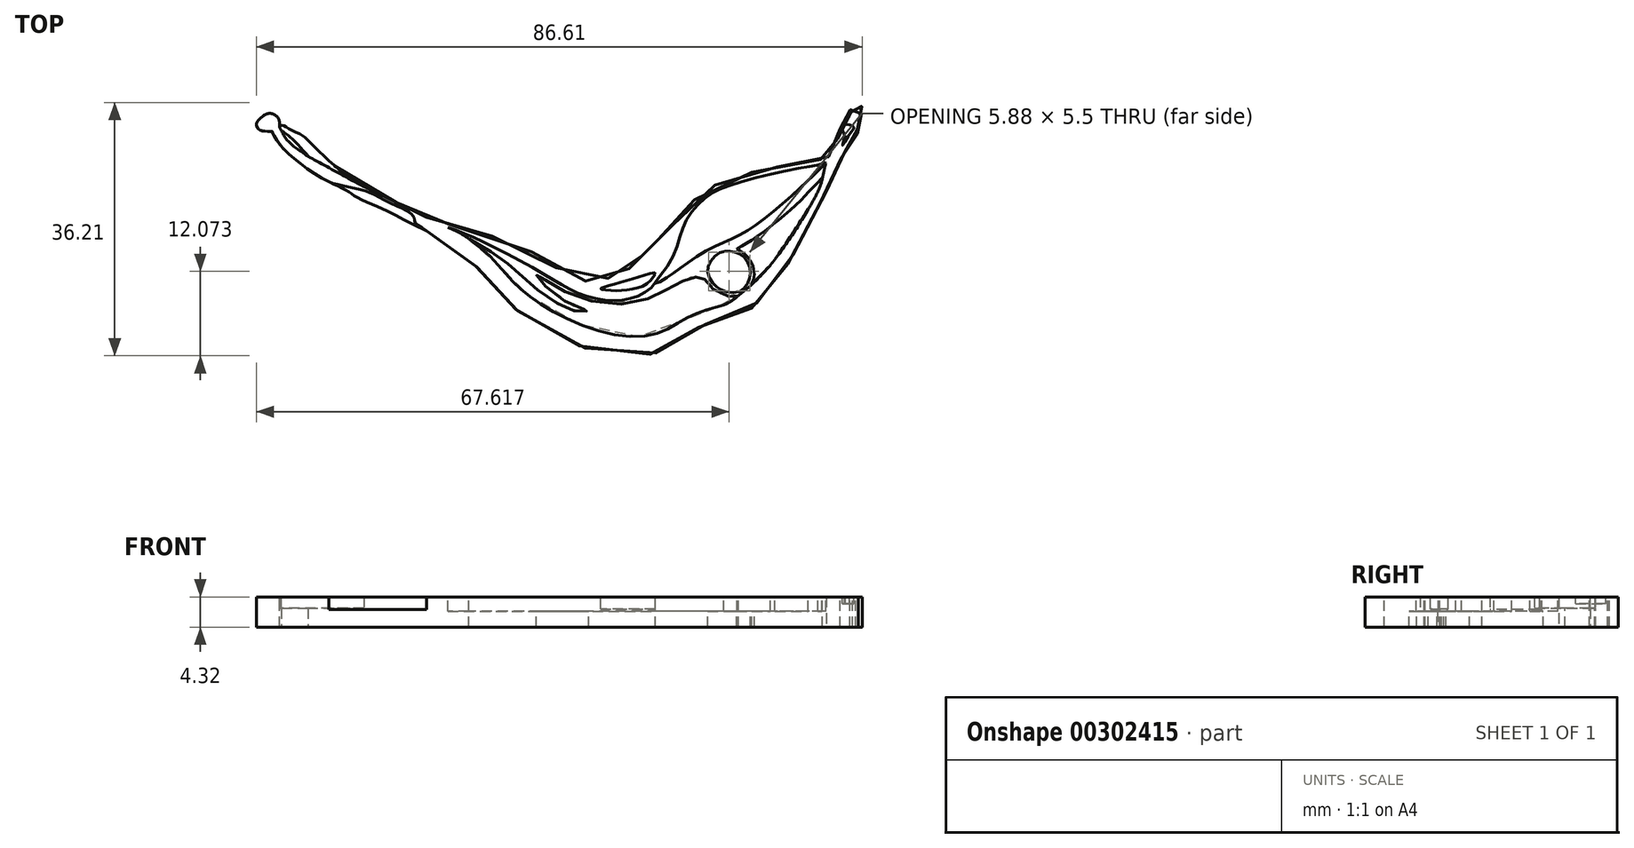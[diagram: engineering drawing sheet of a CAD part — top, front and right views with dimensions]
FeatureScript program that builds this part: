
annotation { "Feature Type Name" : "Feature", "Feature Type Description" : "" }
export const myFeature = defineFeature(function(context is Context, id is Id, definition is map)
    precondition{}
    {
        {
            var Q0;
            Q0=qCreatedBy(makeId("Top.planeOp"),FACE);
            var sketch = newSketch(context, id + "F0", { "sketchPlane" : qUnion([Q0])});
            skFitSpline(sketch, "E0", {"points": [v(-43.46, 14.38) * mm, v(-44.23, 13.82) * mm, v(-44.8, 13.18) * mm, v(-44.82, 12.68) * mm, v(-44.36, 12.07) * mm, v(-43.25, 11.92) * mm, v(-42.68, 11.9) * mm, v(-42.57, 11.9) * mm, v(-42.53, 11.75) * mm, v(-41.7, 10.3) * mm, v(-39.3, 7.87) * mm, v(-34.59, 4.74) * mm, v(-31.85, 3.4) * mm, v(-30.37, 2.4) * mm, v(-26.53, 0.67) * mm, v(-23.64, -0.81) * mm, v(-20.37, -2.4) * mm, v(-17.35, -4.13) * mm, v(-13.45, -7.38) * mm, v(-9.8, -11.5) * mm, v(-7.92, -13.38) * mm, v(-5.1, -15.68) * mm, v(2.66, -19.24) * mm, v(8.89, -20.2) * mm, v(13.19, -19.5) * mm, v(16.5, -17.42) * mm, v(19.24, -15.76) * mm, v(23.96, -14.69) * mm, v(26.11, -13.28) * mm, v(28.6, -10.38) * mm, v(30.9, -7.42) * mm, v(33.51, -2.7) * mm, v(36.14, 2.38) * mm, v(38, 6.37) * mm, v(38.5, 7.84) * mm, v(39, 8.38) * mm, v(39.55, 9.56) * mm, v(40.04, 10.09) * mm, v(40.35, 11.03) * mm, v(41.15, 11.69) * mm, v(41.15, 11.97) * mm, v(40.9, 12.98) * mm, v(40.84, 13.54) * mm, v(40.94, 13.74) * mm, v(41.47, 14.13) * mm, v(41.74, 14.96) * mm, v(41.54, 15.76) * mm, v(40.73, 16) * mm, v(40.18, 15.73) * mm, v(40, 15.17) * mm, v(40.25, 14.82) * mm, v(40.39, 14.68) * mm, v(39.83, 14.68) * mm, v(39.2, 13.81) * mm, v(38.64, 12.7) * mm, v(38.57, 11.58) * mm, v(37.8, 10.12) * mm, v(37.42, 9.29) * mm, v(37.15, 8.48) * mm, v(36.8, 8.2) * mm, v(36.24, 8) * mm, v(32.93, 7.44) * mm, v(26.45, 6.18) * mm, v(22.34, 5) * mm, v(18.2, 2.44) * mm, v(15.35, -0.53) * mm, v(13.74, -2.57) * mm, v(11.52, -4.5) * mm, v(10.67, -5.35) * mm, v(9.53, -6.82) * mm, v(7.86, -8.1) * mm, v(6.39, -8.84) * mm, v(3.57, -9.5) * mm, v(0.75, -9.15) * mm, v(-3.47, -6.61) * mm, v(-7.61, -4.31) * mm, v(-16.63, -1.54) * mm, v(-19.79, -0.7) * mm, v(-23.14, 0.88) * mm, v(-29.1, 3.83) * mm, v(-33.31, 6.66) * mm, v(-37.33, 10.5) * mm, v(-38.62, 11.54) * mm, v(-40.4, 12.37) * mm, v(-41.2, 12.78) * mm, v(-41.53, 12.66) * mm, v(-41.53, 12.96) * mm, v(-41.76, 13.84) * mm, v(-42.64, 14.43) * mm, v(-43.46, 14.38) * mm]});
            skFitSpline(sketch, "E1", {"points": [v(-14.45, -3.47) * mm, v(-11.98, -5.47) * mm, v(-8.6, -9.16) * mm, v(-4.78, -12.4) * mm, v(3.52, -16.48) * mm, v(11.92, -17.15) * mm, v(16.23, -15.05) * mm, v(20, -13.5) * mm, v(22.54, -12.67) * mm, v(23.7, -11.87) * mm, v(24.06, -11.6) * mm, v(23.7, -11.71) * mm, v(23.36, -11.76) * mm, v(22.28, -11.66) * mm, v(20.73, -10.86) * mm, v(19.84, -10.07) * mm, v(19.35, -9.27) * mm, v(19.1, -9.24) * mm, v(18.81, -9.13) * mm, v(18.34, -8.96) * mm, v(17.72, -8.93) * mm, v(16.78, -9.06) * mm, v(15.52, -9.94) * mm, v(13.74, -10.75) * mm, v(12.14, -11.6) * mm, v(9.16, -12.63) * mm, v(4.7, -12.7) * mm, v(0.45, -11.54) * mm, v(-2.41, -10.03) * mm, v(-4.02, -9.05) * mm, v(-4.68, -8.62) * mm, v(-4.8, -8.64) * mm, v(-4.78, -8.75) * mm, v(-4.2, -9.48) * mm, v(-3.27, -10.53) * mm, v(-0.57, -12.48) * mm, v(1.68, -13.47) * mm, v(2.44, -13.62) * mm, v(2.56, -13.66) * mm, v(2.63, -13.74) * mm, v(2.54, -13.8) * mm, v(2.23, -13.85) * mm, v(1.72, -13.87) * mm, v(0.62, -13.77) * mm, v(-0.47, -13.35) * mm, v(-2.89, -12.12) * mm, v(-5.08, -10.42) * mm, v(-6.62, -9.1) * mm, v(-7.7, -7.93) * mm, v(-9.64, -6.52) * mm, v(-11.55, -5.11) * mm, v(-14.45, -3.47) * mm]});
            skFitSpline(sketch, "E2", {"points": [v(12.2, -9.81) * mm, v(14.18, -7) * mm, v(15.74, -3.08) * mm, v(17.1, 0) * mm, v(19.55, 2.56) * mm, v(22.34, 4.02) * mm, v(30.1, 6.1) * mm, v(35.1, 7.05) * mm, v(36.11, 7.31) * mm, v(36.51, 7.45) * mm, v(36.62, 7.48) * mm, v(36.54, 7.38) * mm, v(35.62, 6.44) * mm, v(34.13, 5) * mm, v(30.47, 1.6) * mm, v(26.26, -1.68) * mm, v(23.17, -3.45) * mm, v(19.85, -4.99) * mm, v(15.96, -7.51) * mm, v(13.72, -9.06) * mm, v(12.2, -9.81) * mm]});
            skFitSpline(sketch, "E3", {"points": [v(23.8, -4.96) * mm, v(24.13, -5.1) * mm, v(25.71, -6.5) * mm, v(26.28, -8.03) * mm, v(26.22, -9.26) * mm, v(25.98, -9.9) * mm, v(26.37, -9.55) * mm, v(28.15, -7.77) * mm, v(29.91, -5.54) * mm, v(32.05, -2.29) * mm, v(34.42, 1.4) * mm, v(35.71, 3.98) * mm, v(36.04, 5.01) * mm, v(36.07, 5.2) * mm, v(36.07, 5.3) * mm, v(35.97, 5.22) * mm, v(35.8, 5.01) * mm, v(34.73, 3.9) * mm, v(32.75, 1.82) * mm, v(28.99, -1.45) * mm, v(27.07, -2.89) * mm, v(24.53, -4.52) * mm, v(23.8, -4.96) * mm]});
            skFitSpline(sketch, "E4", {"points": [v(23.56, -5.38) * mm, v(24.75, -5.97) * mm, v(25.7, -7.5) * mm, v(25.71, -8.83) * mm, v(25.2, -10.15) * mm, v(23.8, -11.15) * mm, v(21.76, -10.81) * mm, v(20.69, -10.11) * mm, v(19.78, -8.74) * mm, v(19.86, -7.13) * mm, v(21.02, -5.68) * mm, v(22.4, -5.25) * mm, v(23.56, -5.38) * mm]});
            skFitSpline(sketch, "E5", {"points": [v(-37.48, 8.36) * mm, v(-38.4, 9) * mm, v(-39.47, 9.7) * mm, v(-40.17, 10.38) * mm, v(-40.78, 11.08) * mm, v(-41.2, 11.88) * mm, v(-41.26, 11.99) * mm, v(-41.14, 11.94) * mm, v(-40.59, 11.5) * mm, v(-39.83, 10.94) * mm, v(-38.98, 10.06) * mm, v(-37.87, 8.86) * mm, v(-37.48, 8.36) * mm]});
            skSolve(sketch);
        }
        {
            var Q0;
            Q0=qSketchRegion(id+"F0",true);
            extrude(context, id + "F1", {"entities" : qUnion([Q0]), "depth" : 4.32 * mm});
        }
        {
            var Q0;
            Q0=makeQuery(id+"F1.opExtrude","CAP_FACE",FACE,{"disambiguationData":[OSD([sQuery(id+"F0.wireOp",EDGE,"E0"),sQuery(id+"F0.wireOp",EDGE,"E1"),sQuery(id+"F0.wireOp",EDGE,"E2"),sQuery(id+"F0.wireOp",EDGE,"E3"),sQuery(id+"F0.wireOp",EDGE,"E4"),sQuery(id+"F0.wireOp",EDGE,"E5")])],"isStart":false});
            var sketch = newSketch(context, id + "F2", { "sketchPlane" : qUnion([Q0])});
            skFitSpline(sketch, "E6", {"points": [v(-41.56, 12.7) * mm, v(-41.52, 12.46) * mm, v(-41.26, 11.98) * mm], "startDerivative": vector(0.03, -0.57) * mm, "endDerivative": vector(0.54, -0.86) * mm});
            skFitSpline(sketch, "E7", {"points": [v(-37.55, 8.4) * mm, v(-37.29, 8.23) * mm, v(-35.44, 7.23) * mm, v(-32.92, 5.83) * mm, v(-29.47, 4.04) * mm], "startDerivative": vector(1.64, -0.93) * mm, "endDerivative": vector(9.67, -4.78) * mm});
            skLineSegment(sketch, "E8", {"start": v(-41.56, 12.7) * mm, "end": v(-39.23, 15.85) * mm});
            skLineSegment(sketch, "E9", {"start": v(-39.23, 15.85) * mm, "end": v(-29.46, 12.02) * mm});
            skLineSegment(sketch, "E10", {"start": v(-29.46, 12.02) * mm, "end": v(-29.47, 4.04) * mm});
            skLineSegment(sketch, "E11", {"start": v(-41.26, 11.98) * mm, "end": v(-37.55, 8.4) * mm});
            skSolve(sketch);
        }
        {
            var Q0;
            Q0=qSketchRegion(id+"F2",true);
            extrude(context, id + "F3", {"entities" : qUnion([Q0]), "operationType" : NewBodyOperationType.REMOVE, "oppositeDirection" : true, "depth" : 1.6 * mm});
        }
        {
            var Q0;
            Q0=makeQuery(id+"F1.opExtrude","CAP_FACE",FACE,{"disambiguationData":[OSD([sQuery(id+"F0.wireOp",EDGE,"E0"),sQuery(id+"F0.wireOp",EDGE,"E1"),sQuery(id+"F0.wireOp",EDGE,"E2"),sQuery(id+"F0.wireOp",EDGE,"E3"),sQuery(id+"F0.wireOp",EDGE,"E4"),sQuery(id+"F0.wireOp",EDGE,"E5")])],"isStart":false});
            var sketch = newSketch(context, id + "F4", { "sketchPlane" : qUnion([Q0])});
            skFitSpline(sketch, "E12", {"points": [v(-42.67, 11.63) * mm, v(-42.65, 12.53) * mm, v(-42.93, 13.46) * mm, v(-43.57, 13.78) * mm, v(-44.4, 13.24) * mm, v(-44.37, 12.49) * mm, v(-44.09, 12.19) * mm, v(-42.67, 11.63) * mm]});
            skSolve(sketch);
        }
        {
            var Q0;
            {var subQ0=sQuery(id+"F4.wireOp",EDGE,"E12");var subQ1=makeQuery(id+"F1.opExtrude","CAP_EDGE",EDGE,{"disambiguationData":[OSD([sQuery(id+"F0.wireOp",EDGE,"E0")])],"isStart":false});var subQ2=makeQuery(id+"F4.imprint","INTERSECT",VERTEX,{"disambiguationData":[OD(0.0)],"derivedFrom":[subQ1,subQ0]});Q0=makeQuery(id+"F4.imprint","IMPRINT",FACE,{"disambiguationData":[TD([[makeQuery(id+"F4.imprint","IMPRINT",EDGE,{"disambiguationData":[TD([[subQ2,-1.0]])],"derivedFrom":subQ0}),1.0]])]});}
            var Q1;
            Q1=sQuery(id+"F4.wireOp",EDGE,"E12");
            extrude(context, id + "F5", {"entities" : qUnion([Q0]), "operationType" : NewBodyOperationType.REMOVE, "surfaceEntities" : qUnion([Q1]), "oppositeDirection" : true, "depth" : 1.6 * mm});
        }
        {
            var Q0;
            Q0=makeQuery(id+"F1.opExtrude","CAP_FACE",FACE,{"disambiguationData":[OSD([sQuery(id+"F0.wireOp",EDGE,"E0"),sQuery(id+"F0.wireOp",EDGE,"E1"),sQuery(id+"F0.wireOp",EDGE,"E2"),sQuery(id+"F0.wireOp",EDGE,"E3"),sQuery(id+"F0.wireOp",EDGE,"E4"),sQuery(id+"F0.wireOp",EDGE,"E5")])],"isStart":false});
            var sketch = newSketch(context, id + "F6", { "sketchPlane" : qUnion([Q0])});
            skFitSpline(sketch, "E13", {"points": [v(-34.5, 4.7) * mm, v(-32.52, 4.14) * mm, v(-29.38, 3.41) * mm, v(-27.53, 2.59) * mm, v(-24.1, 0.92) * mm, v(-22.83, 0.25) * mm, v(-22.24, -0.62) * mm, v(-22.12, -1.15) * mm, v(-20.52, -2.32) * mm, v(-19.28, -3.42) * mm, v(-19.28, -3.67) * mm, v(-34.28, -4.1) * mm, v(-46.13, 8) * mm, v(-37.67, 6.07) * mm, v(-34.5, 4.7) * mm]});
            skSolve(sketch);
        }
        {
            var Q0;
            Q0=qSketchRegion(id+"F6",true);
            extrude(context, id + "F7", {"entities" : qUnion([Q0]), "operationType" : NewBodyOperationType.REMOVE, "oppositeDirection" : true, "depth" : 1.78 * mm});
        }
        {
            var Q0;
            Q0=makeQuery(id+"F1.opExtrude","CAP_FACE",FACE,{"disambiguationData":[OSD([sQuery(id+"F0.wireOp",EDGE,"E0"),sQuery(id+"F0.wireOp",EDGE,"E1"),sQuery(id+"F0.wireOp",EDGE,"E2"),sQuery(id+"F0.wireOp",EDGE,"E3"),sQuery(id+"F0.wireOp",EDGE,"E4"),sQuery(id+"F0.wireOp",EDGE,"E5")])],"isStart":false});
            var sketch = newSketch(context, id + "F8", { "sketchPlane" : qUnion([Q0])});
            skFitSpline(sketch, "E14", {"points": [v(-14.45, -3.48) * mm, v(-15.83, -2.58) * mm, v(-17.5, -1.8) * mm, v(-19.84, -0.68) * mm], "startDerivative": vector(-4.45, 3.12) * mm, "endDerivative": vector(-6.33, 3.33) * mm});
            skFitSpline(sketch, "E15", {"points": [v(-17.5, -1.8) * mm, v(-12.53, -3.83) * mm, v(-3.37, -8.75) * mm, v(1.33, -11.3) * mm, v(6.19, -12.3) * mm, v(10, -11.52) * mm, v(12.26, -9.59) * mm], "startDerivative": vector(26.31, -9.77) * mm, "endDerivative": vector(8.56, 17.9) * mm});
            skFitSpline(sketch, "E16", {"points": [v(12.26, -9.59) * mm, v(17.9, -3.92) * mm, v(27.08, 3.73) * mm, v(33.87, 5.94) * mm, v(36.55, 7.4) * mm], "startDerivative": vector(19.72, 19.82) * mm, "endDerivative": vector(14.32, 9.64) * mm});
            skFitSpline(sketch, "E17", {"points": [v(36.55, 7.4) * mm, v(36.06, 5.08) * mm, v(35.44, 3.35) * mm, v(28.6, -7.26) * mm, v(23.84, -11.77) * mm, v(21.96, -12.91) * mm, v(16.18, -13.7) * mm, v(5.65, -15.28) * mm, v(-1.48, -13.62) * mm, v(-8.37, -8.4) * mm, v(-12.04, -5.07) * mm, v(-14.45, -3.48) * mm], "startDerivative": vector(-8.87, -42.52) * mm, "endDerivative": vector(-36.1, 21.51) * mm});
            skSolve(sketch);
        }
        {
            var Q0;
            Q0=qSketchRegion(id+"F8",true);
            var Q1;
            Q1=makeQuery(id+"F8.imprint","IMPRINT",FACE,{"disambiguationData":[TD([[makeQuery(id+"F8.imprint","IMPRINT",EDGE,{"derivedFrom":makeQuery(id+"F1.opExtrude","CAP_EDGE",EDGE,{"disambiguationData":[OSD([sQuery(id+"F0.wireOp",EDGE,"E4")])],"isStart":false})}),-1.0]])]});
            extrude(context, id + "F9", {"entities" : qUnion([Q0, Q1]), "operationType" : NewBodyOperationType.REMOVE, "oppositeDirection" : true, "depth" : 2.06 * mm});
        }
        {
            var Q0;
            Q0=makeQuery(id+"F1.opExtrude","CAP_FACE",FACE,{"disambiguationData":[OSD([sQuery(id+"F0.wireOp",EDGE,"E0"),sQuery(id+"F0.wireOp",EDGE,"E1"),sQuery(id+"F0.wireOp",EDGE,"E2"),sQuery(id+"F0.wireOp",EDGE,"E3"),sQuery(id+"F0.wireOp",EDGE,"E4"),sQuery(id+"F0.wireOp",EDGE,"E5")])],"isStart":false});
            var sketch = newSketch(context, id + "F10", { "sketchPlane" : qUnion([Q0])});
            skFitSpline(sketch, "E18", {"points": [v(6.6, -10.89) * mm, v(8.28, -10.74) * mm, v(10.11, -10.37) * mm, v(11.34, -9.58) * mm, v(12.17, -8.38) * mm, v(10.78, -8.6) * mm, v(8.65, -9.28) * mm, v(6.3, -9.95) * mm, v(4.95, -10.36) * mm, v(4.35, -10.62) * mm, v(4.95, -10.77) * mm, v(6.6, -10.89) * mm]});
            skSolve(sketch);
        }
        {
            var Q0;
            Q0=qSketchRegion(id+"F10",true);
            extrude(context, id + "F11", {"entities" : qUnion([Q0]), "operationType" : NewBodyOperationType.REMOVE, "oppositeDirection" : true, "depth" : 1.75 * mm});
        }
        {
            var Q0;
            Q0=makeQuery(id+"F1.opExtrude","CAP_FACE",FACE,{"disambiguationData":[OSD([sQuery(id+"F0.wireOp",EDGE,"E0"),sQuery(id+"F0.wireOp",EDGE,"E1"),sQuery(id+"F0.wireOp",EDGE,"E2"),sQuery(id+"F0.wireOp",EDGE,"E3"),sQuery(id+"F0.wireOp",EDGE,"E4"),sQuery(id+"F0.wireOp",EDGE,"E5")])],"isStart":false});
            var sketch = newSketch(context, id + "F12", { "sketchPlane" : qUnion([Q0])});
            skFitSpline(sketch, "E19", {"points": [v(39.96, 14.24) * mm, v(39.62, 13.62) * mm, v(39.4, 12.95) * mm, v(40.27, 12.76) * mm, v(40.6, 12.4) * mm, v(40.02, 11.62) * mm, v(38.95, 9.9) * mm, v(39.22, 11) * mm, v(39.04, 11.87) * mm, v(38.9, 12.58) * mm, v(39.2, 13.44) * mm, v(39.96, 14.24) * mm]});
            skSolve(sketch);
        }
        {
            var Q0;
            Q0=makeQuery(id+"F12.imprint","IMPRINT",FACE,{"disambiguationData":[TD([[makeQuery(id+"F12.imprint","IMPRINT",EDGE,{"derivedFrom":sQuery(id+"F12.wireOp",EDGE,"E19")}),-1.0]])]});
            extrude(context, id + "F13", {"entities" : qUnion([Q0]), "operationType" : NewBodyOperationType.REMOVE, "oppositeDirection" : true, "depth" : 0.94 * mm});
        }
    });
